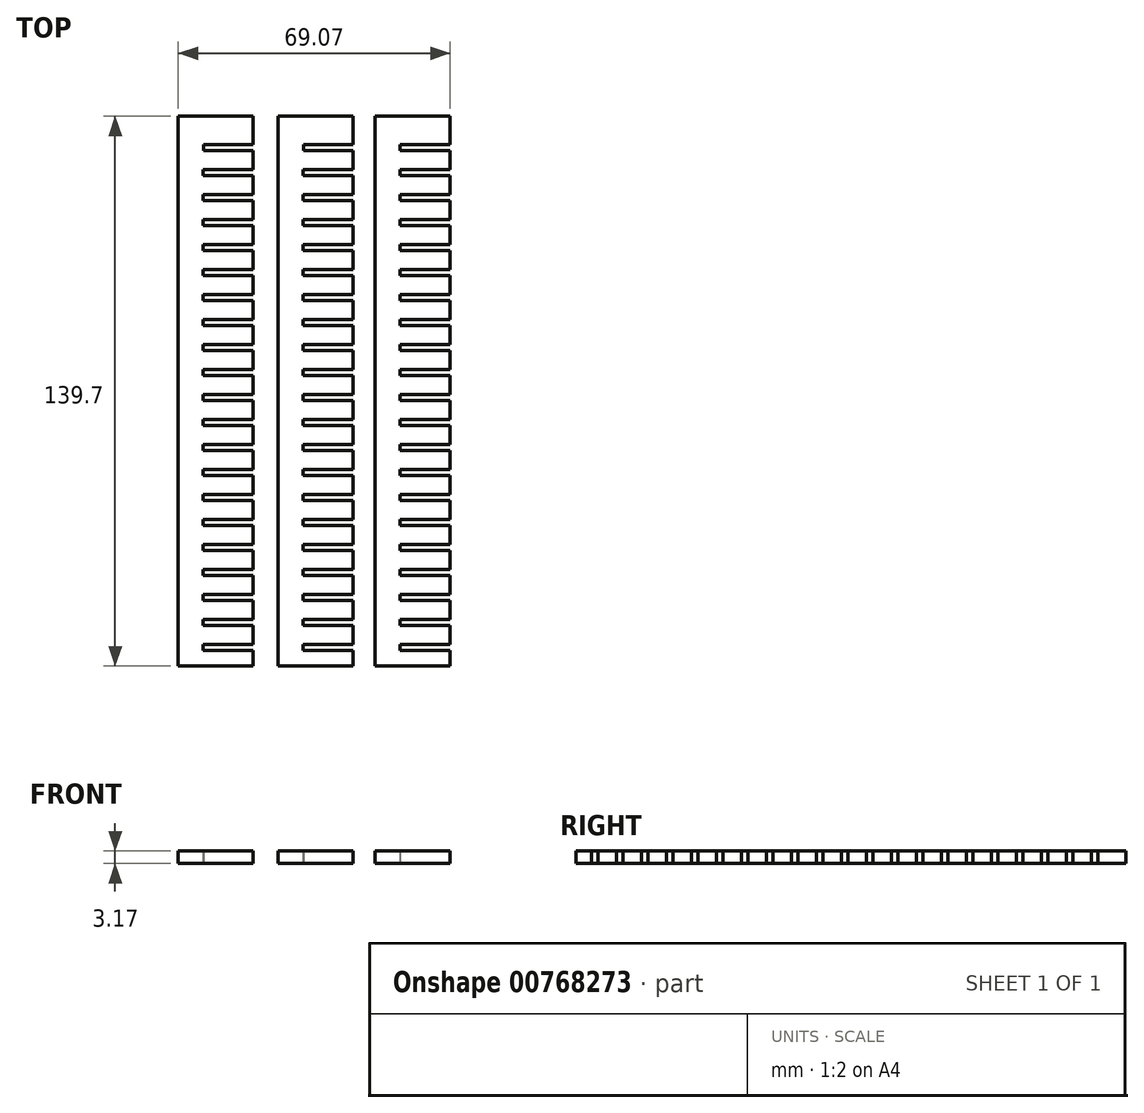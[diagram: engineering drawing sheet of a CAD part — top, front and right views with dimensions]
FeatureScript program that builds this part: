
annotation { "Feature Type Name" : "Feature", "Feature Type Description" : "" }
export const myFeature = defineFeature(function(context is Context, id is Id, definition is map)
    precondition{}
    {
        {
            var Q0;
            Q0=qCreatedBy(makeId("Top.planeOp"),FACE);
            var sketch = newSketch(context, id + "F0", { "sketchPlane" : qUnion([Q0])});
            skLineSegment(sketch, "E0.bottom", {"start": v(0, 0) * mm, "end": v(19.05, 0) * mm});
            skLineSegment(sketch, "E0.top", {"start": v(0, 139.7) * mm, "end": v(19.05, 139.7) * mm});
            skLineSegment(sketch, "E0.left", {"start": v(0, 0) * mm, "end": v(0, 139.7) * mm});
            skLineSegment(sketch, "E0.right", {"start": v(19.05, 0) * mm, "end": v(19.05, 3.96) * mm});
            skLineSegment(sketch, "E1.bottom", {"start": v(19.05, 3.96) * mm, "end": v(6.35, 3.96) * mm});
            skLineSegment(sketch, "E1.top", {"start": v(19.05, 5.55) * mm, "end": v(6.35, 5.55) * mm});
            skLineSegment(sketch, "E1.right", {"start": v(6.35, 3.96) * mm, "end": v(6.35, 5.55) * mm});
            skLineSegment(sketch, "E2.1.0.0", {"start": v(6.35, 10.31) * mm, "end": v(6.35, 11.9) * mm});
            skLineSegment(sketch, "E2.1.0.1", {"start": v(19.05, 10.31) * mm, "end": v(6.35, 10.31) * mm});
            skLineSegment(sketch, "E2.1.0.2", {"start": v(19.05, 11.9) * mm, "end": v(6.35, 11.9) * mm});
            skLineSegment(sketch, "E2.2.0.0", {"start": v(6.35, 16.66) * mm, "end": v(6.35, 18.25) * mm});
            skLineSegment(sketch, "E2.2.0.1", {"start": v(19.05, 16.66) * mm, "end": v(6.35, 16.66) * mm});
            skLineSegment(sketch, "E2.2.0.2", {"start": v(19.05, 18.25) * mm, "end": v(6.35, 18.25) * mm});
            skLineSegment(sketch, "E2.3.0.0", {"start": v(6.35, 23.01) * mm, "end": v(6.35, 24.6) * mm});
            skLineSegment(sketch, "E2.3.0.1", {"start": v(19.05, 23.01) * mm, "end": v(6.35, 23.01) * mm});
            skLineSegment(sketch, "E2.3.0.2", {"start": v(19.05, 24.6) * mm, "end": v(6.35, 24.6) * mm});
            skLineSegment(sketch, "E2.4.0.0", {"start": v(6.35, 29.36) * mm, "end": v(6.35, 30.95) * mm});
            skLineSegment(sketch, "E2.4.0.1", {"start": v(19.05, 29.36) * mm, "end": v(6.35, 29.36) * mm});
            skLineSegment(sketch, "E2.4.0.2", {"start": v(19.05, 30.95) * mm, "end": v(6.35, 30.95) * mm});
            skLineSegment(sketch, "E2.5.0.0", {"start": v(6.35, 35.71) * mm, "end": v(6.35, 37.3) * mm});
            skLineSegment(sketch, "E2.5.0.1", {"start": v(19.05, 35.71) * mm, "end": v(6.35, 35.71) * mm});
            skLineSegment(sketch, "E2.5.0.2", {"start": v(19.05, 37.3) * mm, "end": v(6.35, 37.3) * mm});
            skLineSegment(sketch, "E2.6.0.0", {"start": v(6.35, 42.06) * mm, "end": v(6.35, 43.65) * mm});
            skLineSegment(sketch, "E2.6.0.1", {"start": v(19.05, 42.06) * mm, "end": v(6.35, 42.06) * mm});
            skLineSegment(sketch, "E2.6.0.2", {"start": v(19.05, 43.65) * mm, "end": v(6.35, 43.65) * mm});
            skLineSegment(sketch, "E2.7.0.0", {"start": v(6.35, 48.41) * mm, "end": v(6.35, 50) * mm});
            skLineSegment(sketch, "E2.7.0.1", {"start": v(19.05, 48.41) * mm, "end": v(6.35, 48.41) * mm});
            skLineSegment(sketch, "E2.7.0.2", {"start": v(19.05, 50) * mm, "end": v(6.35, 50) * mm});
            skLineSegment(sketch, "E2.8.0.0", {"start": v(6.35, 54.76) * mm, "end": v(6.35, 56.35) * mm});
            skLineSegment(sketch, "E2.8.0.1", {"start": v(19.05, 54.76) * mm, "end": v(6.35, 54.76) * mm});
            skLineSegment(sketch, "E2.8.0.2", {"start": v(19.05, 56.35) * mm, "end": v(6.35, 56.35) * mm});
            skLineSegment(sketch, "E2.9.0.0", {"start": v(6.35, 61.11) * mm, "end": v(6.35, 62.7) * mm});
            skLineSegment(sketch, "E2.9.0.1", {"start": v(19.05, 61.11) * mm, "end": v(6.35, 61.11) * mm});
            skLineSegment(sketch, "E2.9.0.2", {"start": v(19.05, 62.7) * mm, "end": v(6.35, 62.7) * mm});
            skLineSegment(sketch, "E2.direction1", {"start": v(6.35, 3.96) * mm, "end": v(6.35, 10.31) * mm, "construction": true});
            skLineSegment(sketch, "E3.1.0.0", {"start": v(6.35, 67.46) * mm, "end": v(6.35, 69.05) * mm});
            skLineSegment(sketch, "E3.1.0.1", {"start": v(19.05, 67.46) * mm, "end": v(6.35, 67.46) * mm});
            skLineSegment(sketch, "E3.1.0.2", {"start": v(19.05, 69.05) * mm, "end": v(6.35, 69.05) * mm});
            skLineSegment(sketch, "E3.2.0.0", {"start": v(6.35, 73.81) * mm, "end": v(6.35, 75.4) * mm});
            skLineSegment(sketch, "E3.2.0.1", {"start": v(19.05, 73.81) * mm, "end": v(6.35, 73.81) * mm});
            skLineSegment(sketch, "E3.2.0.2", {"start": v(19.05, 75.4) * mm, "end": v(6.35, 75.4) * mm});
            skLineSegment(sketch, "E3.3.0.0", {"start": v(6.35, 80.16) * mm, "end": v(6.35, 81.75) * mm});
            skLineSegment(sketch, "E3.3.0.1", {"start": v(19.05, 80.16) * mm, "end": v(6.35, 80.16) * mm});
            skLineSegment(sketch, "E3.3.0.2", {"start": v(19.05, 81.75) * mm, "end": v(6.35, 81.75) * mm});
            skLineSegment(sketch, "E3.4.0.0", {"start": v(6.35, 86.51) * mm, "end": v(6.35, 88.1) * mm});
            skLineSegment(sketch, "E3.4.0.1", {"start": v(19.05, 86.51) * mm, "end": v(6.35, 86.51) * mm});
            skLineSegment(sketch, "E3.4.0.2", {"start": v(19.05, 88.1) * mm, "end": v(6.35, 88.1) * mm});
            skLineSegment(sketch, "E3.5.0.0", {"start": v(6.35, 92.86) * mm, "end": v(6.35, 94.45) * mm});
            skLineSegment(sketch, "E3.5.0.1", {"start": v(19.05, 92.86) * mm, "end": v(6.35, 92.86) * mm});
            skLineSegment(sketch, "E3.5.0.2", {"start": v(19.05, 94.45) * mm, "end": v(6.35, 94.45) * mm});
            skLineSegment(sketch, "E3.6.0.0", {"start": v(6.35, 99.21) * mm, "end": v(6.35, 100.8) * mm});
            skLineSegment(sketch, "E3.6.0.1", {"start": v(19.05, 99.21) * mm, "end": v(6.35, 99.21) * mm});
            skLineSegment(sketch, "E3.6.0.2", {"start": v(19.05, 100.8) * mm, "end": v(6.35, 100.8) * mm});
            skLineSegment(sketch, "E3.7.0.0", {"start": v(6.35, 105.56) * mm, "end": v(6.35, 107.15) * mm});
            skLineSegment(sketch, "E3.7.0.1", {"start": v(19.05, 105.56) * mm, "end": v(6.35, 105.56) * mm});
            skLineSegment(sketch, "E3.7.0.2", {"start": v(19.05, 107.15) * mm, "end": v(6.35, 107.15) * mm});
            skLineSegment(sketch, "E3.8.0.0", {"start": v(6.35, 111.91) * mm, "end": v(6.35, 113.5) * mm});
            skLineSegment(sketch, "E3.8.0.1", {"start": v(19.05, 111.91) * mm, "end": v(6.35, 111.91) * mm});
            skLineSegment(sketch, "E3.8.0.2", {"start": v(19.05, 113.5) * mm, "end": v(6.35, 113.5) * mm});
            skLineSegment(sketch, "E3.9.0.0", {"start": v(6.35, 118.26) * mm, "end": v(6.35, 119.85) * mm});
            skLineSegment(sketch, "E3.9.0.1", {"start": v(19.05, 118.26) * mm, "end": v(6.35, 118.26) * mm});
            skLineSegment(sketch, "E3.9.0.2", {"start": v(19.05, 119.85) * mm, "end": v(6.35, 119.85) * mm});
            skLineSegment(sketch, "E3.direction1", {"start": v(6.35, 61.11) * mm, "end": v(6.35, 67.46) * mm, "construction": true});
            skLineSegment(sketch, "E4.1.0.0", {"start": v(6.37, 124.61) * mm, "end": v(6.37, 126.2) * mm});
            skLineSegment(sketch, "E4.1.0.1", {"start": v(19.07, 124.61) * mm, "end": v(6.37, 124.61) * mm});
            skLineSegment(sketch, "E4.1.0.2", {"start": v(19.07, 126.2) * mm, "end": v(6.37, 126.2) * mm});
            skLineSegment(sketch, "E4.2.0.0", {"start": v(6.38, 130.96) * mm, "end": v(6.38, 132.55) * mm});
            skLineSegment(sketch, "E4.2.0.1", {"start": v(19.08, 130.96) * mm, "end": v(6.38, 130.96) * mm});
            skLineSegment(sketch, "E4.2.0.2", {"start": v(19.08, 132.55) * mm, "end": v(6.38, 132.55) * mm});
            skLineSegment(sketch, "E4.direction1", {"start": v(6.35, 118.26) * mm, "end": v(6.37, 124.61) * mm, "construction": true});
            skLineSegment(sketch, "E5.trimOffspring", {"start": v(19.05, 5.55) * mm, "end": v(19.05, 10.31) * mm});
            skLineSegment(sketch, "E6.trimOffspring", {"start": v(19.05, 11.9) * mm, "end": v(19.05, 16.66) * mm});
            skLineSegment(sketch, "E7.trimOffspring", {"start": v(19.05, 18.25) * mm, "end": v(19.05, 23.01) * mm});
            skLineSegment(sketch, "E8.trimOffspring", {"start": v(19.05, 24.6) * mm, "end": v(19.05, 29.36) * mm});
            skLineSegment(sketch, "E9.trimOffspring", {"start": v(19.05, 30.95) * mm, "end": v(19.05, 35.71) * mm});
            skLineSegment(sketch, "E10.trimOffspring", {"start": v(19.05, 37.3) * mm, "end": v(19.05, 42.06) * mm});
            skLineSegment(sketch, "E11.trimOffspring", {"start": v(19.05, 43.65) * mm, "end": v(19.05, 48.41) * mm});
            skLineSegment(sketch, "E12.trimOffspring", {"start": v(19.05, 50) * mm, "end": v(19.05, 54.76) * mm});
            skLineSegment(sketch, "E13.trimOffspring", {"start": v(19.05, 56.35) * mm, "end": v(19.05, 61.11) * mm});
            skLineSegment(sketch, "E14.trimOffspring", {"start": v(19.05, 62.7) * mm, "end": v(19.05, 67.46) * mm});
            skLineSegment(sketch, "E15.trimOffspring", {"start": v(19.05, 69.05) * mm, "end": v(19.05, 73.81) * mm});
            skLineSegment(sketch, "E16.trimOffspring", {"start": v(19.05, 75.4) * mm, "end": v(19.05, 80.16) * mm});
            skLineSegment(sketch, "E17.trimOffspring", {"start": v(19.05, 81.75) * mm, "end": v(19.05, 86.51) * mm});
            skLineSegment(sketch, "E18.trimOffspring", {"start": v(19.05, 88.1) * mm, "end": v(19.05, 92.86) * mm});
            skLineSegment(sketch, "E19.trimOffspring", {"start": v(19.05, 94.45) * mm, "end": v(19.05, 99.21) * mm});
            skLineSegment(sketch, "E20.trimOffspring", {"start": v(19.05, 100.8) * mm, "end": v(19.05, 105.56) * mm});
            skLineSegment(sketch, "E21.trimOffspring", {"start": v(19.05, 107.15) * mm, "end": v(19.05, 111.91) * mm});
            skLineSegment(sketch, "E22.trimOffspring", {"start": v(19.05, 113.5) * mm, "end": v(19.05, 118.26) * mm});
            skLineSegment(sketch, "E23.trimOffspring", {"start": v(19.05, 119.85) * mm, "end": v(19.05, 124.61) * mm});
            skLineSegment(sketch, "E24.trimOffspring", {"start": v(19.05, 126.2) * mm, "end": v(19.05, 130.96) * mm});
            skLineSegment(sketch, "E25.trimOffspring", {"start": v(19.05, 132.55) * mm, "end": v(19.05, 139.7) * mm});
            skLineSegment(sketch, "E26.bottom", {"start": v(25.4, 0) * mm, "end": v(44.45, 0) * mm});
            skLineSegment(sketch, "E26.top", {"start": v(25.4, 139.7) * mm, "end": v(44.45, 139.7) * mm});
            skLineSegment(sketch, "E26.left", {"start": v(25.4, 0) * mm, "end": v(25.4, 139.7) * mm});
            skLineSegment(sketch, "E26.right", {"start": v(44.45, 0) * mm, "end": v(44.45, 3.96) * mm});
            skLineSegment(sketch, "E27.bottom", {"start": v(44.45, 3.96) * mm, "end": v(31.75, 3.96) * mm});
            skLineSegment(sketch, "E27.top", {"start": v(44.45, 5.55) * mm, "end": v(31.75, 5.55) * mm});
            skLineSegment(sketch, "E27.right", {"start": v(31.75, 3.96) * mm, "end": v(31.75, 5.55) * mm});
            skLineSegment(sketch, "E28.1.0.0", {"start": v(31.75, 10.31) * mm, "end": v(31.75, 11.9) * mm});
            skLineSegment(sketch, "E28.1.0.1", {"start": v(44.45, 10.31) * mm, "end": v(31.75, 10.31) * mm});
            skLineSegment(sketch, "E28.1.0.2", {"start": v(44.45, 11.9) * mm, "end": v(31.75, 11.9) * mm});
            skLineSegment(sketch, "E28.2.0.0", {"start": v(31.75, 16.66) * mm, "end": v(31.75, 18.25) * mm});
            skLineSegment(sketch, "E28.2.0.1", {"start": v(44.45, 16.66) * mm, "end": v(31.75, 16.66) * mm});
            skLineSegment(sketch, "E28.2.0.2", {"start": v(44.45, 18.25) * mm, "end": v(31.75, 18.25) * mm});
            skLineSegment(sketch, "E28.3.0.0", {"start": v(31.75, 23.01) * mm, "end": v(31.75, 24.6) * mm});
            skLineSegment(sketch, "E28.3.0.1", {"start": v(44.45, 23.01) * mm, "end": v(31.75, 23.01) * mm});
            skLineSegment(sketch, "E28.3.0.2", {"start": v(44.45, 24.6) * mm, "end": v(31.75, 24.6) * mm});
            skLineSegment(sketch, "E28.4.0.0", {"start": v(31.75, 29.36) * mm, "end": v(31.75, 30.95) * mm});
            skLineSegment(sketch, "E28.4.0.1", {"start": v(44.45, 29.36) * mm, "end": v(31.75, 29.36) * mm});
            skLineSegment(sketch, "E28.4.0.2", {"start": v(44.45, 30.95) * mm, "end": v(31.75, 30.95) * mm});
            skLineSegment(sketch, "E28.5.0.0", {"start": v(31.75, 35.71) * mm, "end": v(31.75, 37.3) * mm});
            skLineSegment(sketch, "E28.5.0.1", {"start": v(44.45, 35.71) * mm, "end": v(31.75, 35.71) * mm});
            skLineSegment(sketch, "E28.5.0.2", {"start": v(44.45, 37.3) * mm, "end": v(31.75, 37.3) * mm});
            skLineSegment(sketch, "E28.6.0.0", {"start": v(31.75, 42.06) * mm, "end": v(31.75, 43.65) * mm});
            skLineSegment(sketch, "E28.6.0.1", {"start": v(44.45, 42.06) * mm, "end": v(31.75, 42.06) * mm});
            skLineSegment(sketch, "E28.6.0.2", {"start": v(44.45, 43.65) * mm, "end": v(31.75, 43.65) * mm});
            skLineSegment(sketch, "E28.7.0.0", {"start": v(31.75, 48.41) * mm, "end": v(31.75, 50) * mm});
            skLineSegment(sketch, "E28.7.0.1", {"start": v(44.45, 48.41) * mm, "end": v(31.75, 48.41) * mm});
            skLineSegment(sketch, "E28.7.0.2", {"start": v(44.45, 50) * mm, "end": v(31.75, 50) * mm});
            skLineSegment(sketch, "E28.8.0.0", {"start": v(31.75, 54.76) * mm, "end": v(31.75, 56.35) * mm});
            skLineSegment(sketch, "E28.8.0.1", {"start": v(44.45, 54.76) * mm, "end": v(31.75, 54.76) * mm});
            skLineSegment(sketch, "E28.8.0.2", {"start": v(44.45, 56.35) * mm, "end": v(31.75, 56.35) * mm});
            skLineSegment(sketch, "E28.9.0.0", {"start": v(31.75, 61.11) * mm, "end": v(31.75, 62.7) * mm});
            skLineSegment(sketch, "E28.9.0.1", {"start": v(44.45, 61.11) * mm, "end": v(31.75, 61.11) * mm});
            skLineSegment(sketch, "E28.9.0.2", {"start": v(44.45, 62.7) * mm, "end": v(31.75, 62.7) * mm});
            skLineSegment(sketch, "E28.direction1", {"start": v(31.75, 3.96) * mm, "end": v(31.75, 10.31) * mm, "construction": true});
            skLineSegment(sketch, "E29.1.0.0", {"start": v(31.75, 67.46) * mm, "end": v(31.75, 69.05) * mm});
            skLineSegment(sketch, "E29.1.0.1", {"start": v(44.45, 67.46) * mm, "end": v(31.75, 67.46) * mm});
            skLineSegment(sketch, "E29.1.0.2", {"start": v(44.45, 69.05) * mm, "end": v(31.75, 69.05) * mm});
            skLineSegment(sketch, "E29.2.0.0", {"start": v(31.75, 73.81) * mm, "end": v(31.75, 75.4) * mm});
            skLineSegment(sketch, "E29.2.0.1", {"start": v(44.45, 73.81) * mm, "end": v(31.75, 73.81) * mm});
            skLineSegment(sketch, "E29.2.0.2", {"start": v(44.45, 75.4) * mm, "end": v(31.75, 75.4) * mm});
            skLineSegment(sketch, "E29.3.0.0", {"start": v(31.75, 80.16) * mm, "end": v(31.75, 81.75) * mm});
            skLineSegment(sketch, "E29.3.0.1", {"start": v(44.45, 80.16) * mm, "end": v(31.75, 80.16) * mm});
            skLineSegment(sketch, "E29.3.0.2", {"start": v(44.45, 81.75) * mm, "end": v(31.75, 81.75) * mm});
            skLineSegment(sketch, "E29.4.0.0", {"start": v(31.75, 86.51) * mm, "end": v(31.75, 88.1) * mm});
            skLineSegment(sketch, "E29.4.0.1", {"start": v(44.45, 86.51) * mm, "end": v(31.75, 86.51) * mm});
            skLineSegment(sketch, "E29.4.0.2", {"start": v(44.45, 88.1) * mm, "end": v(31.75, 88.1) * mm});
            skLineSegment(sketch, "E29.5.0.0", {"start": v(31.75, 92.86) * mm, "end": v(31.75, 94.45) * mm});
            skLineSegment(sketch, "E29.5.0.1", {"start": v(44.45, 92.86) * mm, "end": v(31.75, 92.86) * mm});
            skLineSegment(sketch, "E29.5.0.2", {"start": v(44.45, 94.45) * mm, "end": v(31.75, 94.45) * mm});
            skLineSegment(sketch, "E29.6.0.0", {"start": v(31.75, 99.21) * mm, "end": v(31.75, 100.8) * mm});
            skLineSegment(sketch, "E29.6.0.1", {"start": v(44.45, 99.21) * mm, "end": v(31.75, 99.21) * mm});
            skLineSegment(sketch, "E29.6.0.2", {"start": v(44.45, 100.8) * mm, "end": v(31.75, 100.8) * mm});
            skLineSegment(sketch, "E29.7.0.0", {"start": v(31.75, 105.56) * mm, "end": v(31.75, 107.15) * mm});
            skLineSegment(sketch, "E29.7.0.1", {"start": v(44.45, 105.56) * mm, "end": v(31.75, 105.56) * mm});
            skLineSegment(sketch, "E29.7.0.2", {"start": v(44.45, 107.15) * mm, "end": v(31.75, 107.15) * mm});
            skLineSegment(sketch, "E29.8.0.0", {"start": v(31.75, 111.91) * mm, "end": v(31.75, 113.5) * mm});
            skLineSegment(sketch, "E29.8.0.1", {"start": v(44.45, 111.91) * mm, "end": v(31.75, 111.91) * mm});
            skLineSegment(sketch, "E29.8.0.2", {"start": v(44.45, 113.5) * mm, "end": v(31.75, 113.5) * mm});
            skLineSegment(sketch, "E29.9.0.0", {"start": v(31.75, 118.26) * mm, "end": v(31.75, 119.85) * mm});
            skLineSegment(sketch, "E29.9.0.1", {"start": v(44.45, 118.26) * mm, "end": v(31.75, 118.26) * mm});
            skLineSegment(sketch, "E29.9.0.2", {"start": v(44.45, 119.85) * mm, "end": v(31.75, 119.85) * mm});
            skLineSegment(sketch, "E29.direction1", {"start": v(31.75, 61.11) * mm, "end": v(31.75, 67.46) * mm, "construction": true});
            skLineSegment(sketch, "E30.1.0.0", {"start": v(31.77, 124.61) * mm, "end": v(31.77, 126.2) * mm});
            skLineSegment(sketch, "E30.1.0.1", {"start": v(44.47, 124.61) * mm, "end": v(31.77, 124.61) * mm});
            skLineSegment(sketch, "E30.1.0.2", {"start": v(44.47, 126.2) * mm, "end": v(31.77, 126.2) * mm});
            skLineSegment(sketch, "E30.2.0.0", {"start": v(31.78, 130.96) * mm, "end": v(31.78, 132.55) * mm});
            skLineSegment(sketch, "E30.2.0.1", {"start": v(44.48, 130.96) * mm, "end": v(31.78, 130.96) * mm});
            skLineSegment(sketch, "E30.2.0.2", {"start": v(44.48, 132.55) * mm, "end": v(31.78, 132.55) * mm});
            skLineSegment(sketch, "E30.direction1", {"start": v(31.75, 118.26) * mm, "end": v(31.77, 124.61) * mm, "construction": true});
            skLineSegment(sketch, "E31.trimOffspring", {"start": v(44.45, 5.55) * mm, "end": v(44.45, 10.31) * mm});
            skLineSegment(sketch, "E32.trimOffspring", {"start": v(44.45, 11.9) * mm, "end": v(44.45, 16.66) * mm});
            skLineSegment(sketch, "E33.trimOffspring", {"start": v(44.45, 18.25) * mm, "end": v(44.45, 23.01) * mm});
            skLineSegment(sketch, "E34.trimOffspring", {"start": v(44.45, 24.6) * mm, "end": v(44.45, 29.36) * mm});
            skLineSegment(sketch, "E35.trimOffspring", {"start": v(44.45, 30.95) * mm, "end": v(44.45, 35.71) * mm});
            skLineSegment(sketch, "E36.trimOffspring", {"start": v(44.45, 37.3) * mm, "end": v(44.45, 42.06) * mm});
            skLineSegment(sketch, "E37.trimOffspring", {"start": v(44.45, 43.65) * mm, "end": v(44.45, 48.41) * mm});
            skLineSegment(sketch, "E38.trimOffspring", {"start": v(44.45, 50) * mm, "end": v(44.45, 54.76) * mm});
            skLineSegment(sketch, "E39.trimOffspring", {"start": v(44.45, 56.35) * mm, "end": v(44.45, 61.11) * mm});
            skLineSegment(sketch, "E40.trimOffspring", {"start": v(44.45, 62.7) * mm, "end": v(44.45, 67.46) * mm});
            skLineSegment(sketch, "E41.trimOffspring", {"start": v(44.45, 69.05) * mm, "end": v(44.45, 73.81) * mm});
            skLineSegment(sketch, "E42.trimOffspring", {"start": v(44.45, 75.4) * mm, "end": v(44.45, 80.16) * mm});
            skLineSegment(sketch, "E43.trimOffspring", {"start": v(44.45, 81.75) * mm, "end": v(44.45, 86.51) * mm});
            skLineSegment(sketch, "E44.trimOffspring", {"start": v(44.45, 88.1) * mm, "end": v(44.45, 92.86) * mm});
            skLineSegment(sketch, "E45.trimOffspring", {"start": v(44.45, 94.45) * mm, "end": v(44.45, 99.21) * mm});
            skLineSegment(sketch, "E46.trimOffspring", {"start": v(44.45, 100.8) * mm, "end": v(44.45, 105.56) * mm});
            skLineSegment(sketch, "E47.trimOffspring", {"start": v(44.45, 107.15) * mm, "end": v(44.45, 111.91) * mm});
            skLineSegment(sketch, "E48.trimOffspring", {"start": v(44.45, 113.5) * mm, "end": v(44.45, 118.26) * mm});
            skLineSegment(sketch, "E49.trimOffspring", {"start": v(44.45, 119.85) * mm, "end": v(44.45, 124.61) * mm});
            skLineSegment(sketch, "E50.trimOffspring", {"start": v(44.45, 126.2) * mm, "end": v(44.45, 130.96) * mm});
            skLineSegment(sketch, "E51.trimOffspring", {"start": v(44.45, 132.55) * mm, "end": v(44.45, 139.7) * mm});
            skLineSegment(sketch, "E52.bottom", {"start": v(50.02, 0) * mm, "end": v(69.07, 0) * mm});
            skLineSegment(sketch, "E52.top", {"start": v(50.02, 139.7) * mm, "end": v(69.07, 139.7) * mm});
            skLineSegment(sketch, "E52.left", {"start": v(50.02, 0) * mm, "end": v(50.02, 139.7) * mm});
            skLineSegment(sketch, "E52.right", {"start": v(69.07, 0) * mm, "end": v(69.07, 3.96) * mm});
            skLineSegment(sketch, "E53.bottom", {"start": v(69.07, 3.96) * mm, "end": v(56.37, 3.96) * mm});
            skLineSegment(sketch, "E53.top", {"start": v(69.07, 5.55) * mm, "end": v(56.37, 5.55) * mm});
            skLineSegment(sketch, "E53.right", {"start": v(56.37, 3.96) * mm, "end": v(56.37, 5.55) * mm});
            skLineSegment(sketch, "E54.1.0.0", {"start": v(56.37, 10.31) * mm, "end": v(56.37, 11.9) * mm});
            skLineSegment(sketch, "E54.1.0.1", {"start": v(69.07, 10.31) * mm, "end": v(56.37, 10.31) * mm});
            skLineSegment(sketch, "E54.1.0.2", {"start": v(69.07, 11.9) * mm, "end": v(56.37, 11.9) * mm});
            skLineSegment(sketch, "E54.2.0.0", {"start": v(56.37, 16.66) * mm, "end": v(56.37, 18.25) * mm});
            skLineSegment(sketch, "E54.2.0.1", {"start": v(69.07, 16.66) * mm, "end": v(56.37, 16.66) * mm});
            skLineSegment(sketch, "E54.2.0.2", {"start": v(69.07, 18.25) * mm, "end": v(56.37, 18.25) * mm});
            skLineSegment(sketch, "E54.3.0.0", {"start": v(56.37, 23.01) * mm, "end": v(56.37, 24.6) * mm});
            skLineSegment(sketch, "E54.3.0.1", {"start": v(69.07, 23.01) * mm, "end": v(56.37, 23.01) * mm});
            skLineSegment(sketch, "E54.3.0.2", {"start": v(69.07, 24.6) * mm, "end": v(56.37, 24.6) * mm});
            skLineSegment(sketch, "E54.4.0.0", {"start": v(56.37, 29.36) * mm, "end": v(56.37, 30.95) * mm});
            skLineSegment(sketch, "E54.4.0.1", {"start": v(69.07, 29.36) * mm, "end": v(56.37, 29.36) * mm});
            skLineSegment(sketch, "E54.4.0.2", {"start": v(69.07, 30.95) * mm, "end": v(56.37, 30.95) * mm});
            skLineSegment(sketch, "E54.5.0.0", {"start": v(56.37, 35.71) * mm, "end": v(56.37, 37.3) * mm});
            skLineSegment(sketch, "E54.5.0.1", {"start": v(69.07, 35.71) * mm, "end": v(56.37, 35.71) * mm});
            skLineSegment(sketch, "E54.5.0.2", {"start": v(69.07, 37.3) * mm, "end": v(56.37, 37.3) * mm});
            skLineSegment(sketch, "E54.6.0.0", {"start": v(56.37, 42.06) * mm, "end": v(56.37, 43.65) * mm});
            skLineSegment(sketch, "E54.6.0.1", {"start": v(69.07, 42.06) * mm, "end": v(56.37, 42.06) * mm});
            skLineSegment(sketch, "E54.6.0.2", {"start": v(69.07, 43.65) * mm, "end": v(56.37, 43.65) * mm});
            skLineSegment(sketch, "E54.7.0.0", {"start": v(56.37, 48.41) * mm, "end": v(56.37, 50) * mm});
            skLineSegment(sketch, "E54.7.0.1", {"start": v(69.07, 48.41) * mm, "end": v(56.37, 48.41) * mm});
            skLineSegment(sketch, "E54.7.0.2", {"start": v(69.07, 50) * mm, "end": v(56.37, 50) * mm});
            skLineSegment(sketch, "E54.8.0.0", {"start": v(56.37, 54.76) * mm, "end": v(56.37, 56.35) * mm});
            skLineSegment(sketch, "E54.8.0.1", {"start": v(69.07, 54.76) * mm, "end": v(56.37, 54.76) * mm});
            skLineSegment(sketch, "E54.8.0.2", {"start": v(69.07, 56.35) * mm, "end": v(56.37, 56.35) * mm});
            skLineSegment(sketch, "E54.9.0.0", {"start": v(56.37, 61.11) * mm, "end": v(56.37, 62.7) * mm});
            skLineSegment(sketch, "E54.9.0.1", {"start": v(69.07, 61.11) * mm, "end": v(56.37, 61.11) * mm});
            skLineSegment(sketch, "E54.9.0.2", {"start": v(69.07, 62.7) * mm, "end": v(56.37, 62.7) * mm});
            skLineSegment(sketch, "E54.direction1", {"start": v(56.37, 3.96) * mm, "end": v(56.37, 10.31) * mm, "construction": true});
            skLineSegment(sketch, "E55.1.0.0", {"start": v(56.37, 67.46) * mm, "end": v(56.37, 69.05) * mm});
            skLineSegment(sketch, "E55.1.0.1", {"start": v(69.07, 67.46) * mm, "end": v(56.37, 67.46) * mm});
            skLineSegment(sketch, "E55.1.0.2", {"start": v(69.07, 69.05) * mm, "end": v(56.37, 69.05) * mm});
            skLineSegment(sketch, "E55.2.0.0", {"start": v(56.37, 73.81) * mm, "end": v(56.37, 75.4) * mm});
            skLineSegment(sketch, "E55.2.0.1", {"start": v(69.07, 73.81) * mm, "end": v(56.37, 73.81) * mm});
            skLineSegment(sketch, "E55.2.0.2", {"start": v(69.07, 75.4) * mm, "end": v(56.37, 75.4) * mm});
            skLineSegment(sketch, "E55.3.0.0", {"start": v(56.37, 80.16) * mm, "end": v(56.37, 81.75) * mm});
            skLineSegment(sketch, "E55.3.0.1", {"start": v(69.07, 80.16) * mm, "end": v(56.37, 80.16) * mm});
            skLineSegment(sketch, "E55.3.0.2", {"start": v(69.07, 81.75) * mm, "end": v(56.37, 81.75) * mm});
            skLineSegment(sketch, "E55.4.0.0", {"start": v(56.37, 86.51) * mm, "end": v(56.37, 88.1) * mm});
            skLineSegment(sketch, "E55.4.0.1", {"start": v(69.07, 86.51) * mm, "end": v(56.37, 86.51) * mm});
            skLineSegment(sketch, "E55.4.0.2", {"start": v(69.07, 88.1) * mm, "end": v(56.37, 88.1) * mm});
            skLineSegment(sketch, "E55.5.0.0", {"start": v(56.37, 92.86) * mm, "end": v(56.37, 94.45) * mm});
            skLineSegment(sketch, "E55.5.0.1", {"start": v(69.07, 92.86) * mm, "end": v(56.37, 92.86) * mm});
            skLineSegment(sketch, "E55.5.0.2", {"start": v(69.07, 94.45) * mm, "end": v(56.37, 94.45) * mm});
            skLineSegment(sketch, "E55.6.0.0", {"start": v(56.37, 99.21) * mm, "end": v(56.37, 100.8) * mm});
            skLineSegment(sketch, "E55.6.0.1", {"start": v(69.07, 99.21) * mm, "end": v(56.37, 99.21) * mm});
            skLineSegment(sketch, "E55.6.0.2", {"start": v(69.07, 100.8) * mm, "end": v(56.37, 100.8) * mm});
            skLineSegment(sketch, "E55.7.0.0", {"start": v(56.37, 105.56) * mm, "end": v(56.37, 107.15) * mm});
            skLineSegment(sketch, "E55.7.0.1", {"start": v(69.07, 105.56) * mm, "end": v(56.37, 105.56) * mm});
            skLineSegment(sketch, "E55.7.0.2", {"start": v(69.07, 107.15) * mm, "end": v(56.37, 107.15) * mm});
            skLineSegment(sketch, "E55.8.0.0", {"start": v(56.37, 111.91) * mm, "end": v(56.37, 113.5) * mm});
            skLineSegment(sketch, "E55.8.0.1", {"start": v(69.07, 111.91) * mm, "end": v(56.37, 111.91) * mm});
            skLineSegment(sketch, "E55.8.0.2", {"start": v(69.07, 113.5) * mm, "end": v(56.37, 113.5) * mm});
            skLineSegment(sketch, "E55.9.0.0", {"start": v(56.37, 118.26) * mm, "end": v(56.37, 119.85) * mm});
            skLineSegment(sketch, "E55.9.0.1", {"start": v(69.07, 118.26) * mm, "end": v(56.37, 118.26) * mm});
            skLineSegment(sketch, "E55.9.0.2", {"start": v(69.07, 119.85) * mm, "end": v(56.37, 119.85) * mm});
            skLineSegment(sketch, "E55.direction1", {"start": v(56.37, 61.11) * mm, "end": v(56.37, 67.46) * mm, "construction": true});
            skLineSegment(sketch, "E56.1.0.0", {"start": v(56.39, 124.61) * mm, "end": v(56.39, 126.2) * mm});
            skLineSegment(sketch, "E56.1.0.1", {"start": v(69.09, 124.61) * mm, "end": v(56.39, 124.61) * mm});
            skLineSegment(sketch, "E56.1.0.2", {"start": v(69.09, 126.2) * mm, "end": v(56.39, 126.2) * mm});
            skLineSegment(sketch, "E56.2.0.0", {"start": v(56.4, 130.96) * mm, "end": v(56.4, 132.55) * mm});
            skLineSegment(sketch, "E56.2.0.1", {"start": v(69.1, 130.96) * mm, "end": v(56.4, 130.96) * mm});
            skLineSegment(sketch, "E56.2.0.2", {"start": v(69.1, 132.55) * mm, "end": v(56.4, 132.55) * mm});
            skLineSegment(sketch, "E56.direction1", {"start": v(56.37, 118.26) * mm, "end": v(56.39, 124.61) * mm, "construction": true});
            skLineSegment(sketch, "E57.trimOffspring", {"start": v(69.07, 5.55) * mm, "end": v(69.07, 10.31) * mm});
            skLineSegment(sketch, "E58.trimOffspring", {"start": v(69.07, 11.9) * mm, "end": v(69.07, 16.66) * mm});
            skLineSegment(sketch, "E59.trimOffspring", {"start": v(69.07, 18.25) * mm, "end": v(69.07, 23.01) * mm});
            skLineSegment(sketch, "E60.trimOffspring", {"start": v(69.07, 24.6) * mm, "end": v(69.07, 29.36) * mm});
            skLineSegment(sketch, "E61.trimOffspring", {"start": v(69.07, 30.95) * mm, "end": v(69.07, 35.71) * mm});
            skLineSegment(sketch, "E62.trimOffspring", {"start": v(69.07, 37.3) * mm, "end": v(69.07, 42.06) * mm});
            skLineSegment(sketch, "E63.trimOffspring", {"start": v(69.07, 43.65) * mm, "end": v(69.07, 48.41) * mm});
            skLineSegment(sketch, "E64.trimOffspring", {"start": v(69.07, 50) * mm, "end": v(69.07, 54.76) * mm});
            skLineSegment(sketch, "E65.trimOffspring", {"start": v(69.07, 56.35) * mm, "end": v(69.07, 61.11) * mm});
            skLineSegment(sketch, "E66.trimOffspring", {"start": v(69.07, 62.7) * mm, "end": v(69.07, 67.46) * mm});
            skLineSegment(sketch, "E67.trimOffspring", {"start": v(69.07, 69.05) * mm, "end": v(69.07, 73.81) * mm});
            skLineSegment(sketch, "E68.trimOffspring", {"start": v(69.07, 75.4) * mm, "end": v(69.07, 80.16) * mm});
            skLineSegment(sketch, "E69.trimOffspring", {"start": v(69.07, 81.75) * mm, "end": v(69.07, 86.51) * mm});
            skLineSegment(sketch, "E70.trimOffspring", {"start": v(69.07, 88.1) * mm, "end": v(69.07, 92.86) * mm});
            skLineSegment(sketch, "E71.trimOffspring", {"start": v(69.07, 94.45) * mm, "end": v(69.07, 99.21) * mm});
            skLineSegment(sketch, "E72.trimOffspring", {"start": v(69.07, 100.8) * mm, "end": v(69.07, 105.56) * mm});
            skLineSegment(sketch, "E73.trimOffspring", {"start": v(69.07, 107.15) * mm, "end": v(69.07, 111.91) * mm});
            skLineSegment(sketch, "E74.trimOffspring", {"start": v(69.07, 113.5) * mm, "end": v(69.07, 118.26) * mm});
            skLineSegment(sketch, "E75.trimOffspring", {"start": v(69.07, 119.85) * mm, "end": v(69.07, 124.61) * mm});
            skLineSegment(sketch, "E76.trimOffspring", {"start": v(69.07, 126.2) * mm, "end": v(69.07, 130.96) * mm});
            skLineSegment(sketch, "E77.trimOffspring", {"start": v(69.07, 132.55) * mm, "end": v(69.07, 139.7) * mm});
            skSolve(sketch);
        }
        {
            var Q0;
            Q0=makeQuery(id+"F0.imprint","IMPRINT",FACE,{"disambiguationData":[TD([[makeQuery(id+"F0.imprint","IMPRINT",EDGE,{"derivedFrom":sQuery(id+"F0.wireOp",EDGE,"E0.bottom")}),1.0]])]});
            var Q1;
            Q1=makeQuery(id+"F0.imprint","IMPRINT",FACE,{"disambiguationData":[TD([[makeQuery(id+"F0.imprint","IMPRINT",EDGE,{"derivedFrom":sQuery(id+"F0.wireOp",EDGE,"E26.bottom")}),1.0]])]});
            var Q2;
            Q2=makeQuery(id+"F0.imprint","IMPRINT",FACE,{"disambiguationData":[TD([[makeQuery(id+"F0.imprint","IMPRINT",EDGE,{"derivedFrom":sQuery(id+"F0.wireOp",EDGE,"E52.bottom")}),1.0]])]});
            extrude(context, id + "F1", {"entities" : qUnion([Q0, Q1, Q2]), "depth" : 3.17 * mm, "offsetDistance" : 25.4 * mm});
        }
    });
